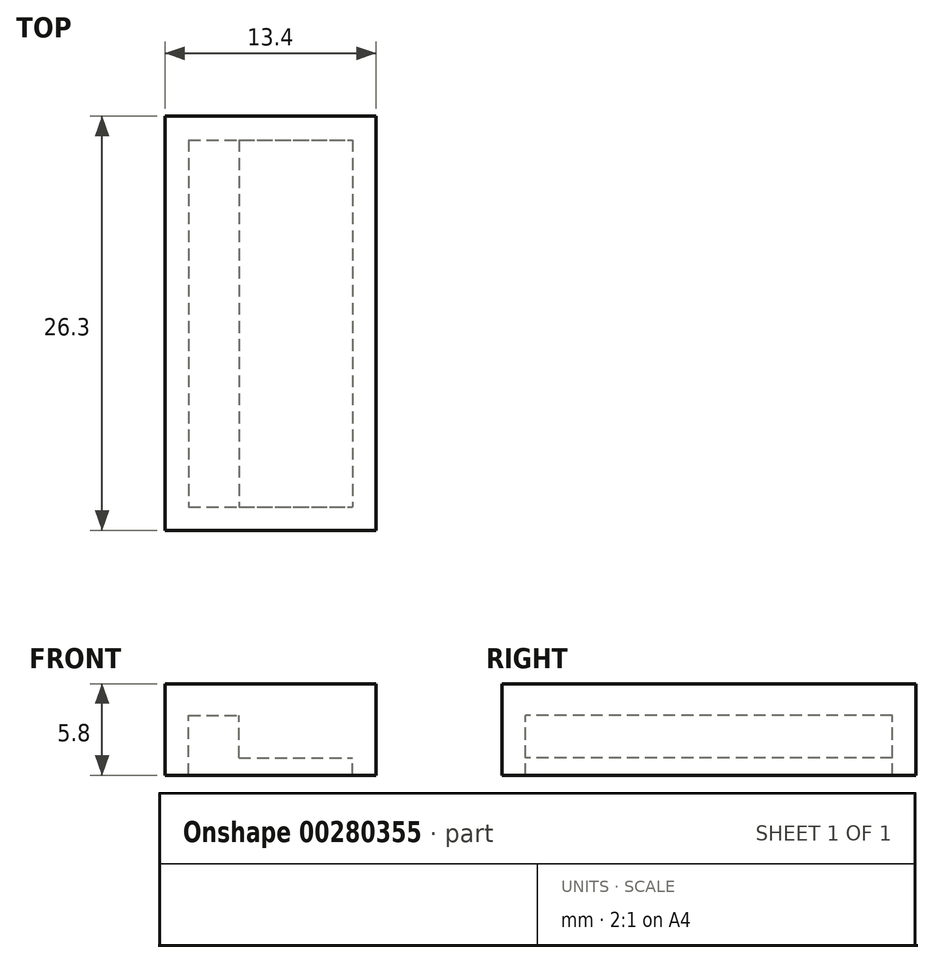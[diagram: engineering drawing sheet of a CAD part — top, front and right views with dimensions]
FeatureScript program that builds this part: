
annotation { "Feature Type Name" : "Feature", "Feature Type Description" : "" }
export const myFeature = defineFeature(function(context is Context, id is Id, definition is map)
    precondition{}
    {
        {
            var Q0;
            Q0=qCreatedBy(makeId("Top.planeOp"),FACE);
            var sketch = newSketch(context, id + "F0", { "sketchPlane" : qUnion([Q0])});
            skLineSegment(sketch, "E0.bottom", {"start": v(-19.84, -7.55) * mm, "end": v(-9.44, -7.55) * mm});
            skLineSegment(sketch, "E0.top", {"start": v(-19.84, -30.85) * mm, "end": v(-9.44, -30.85) * mm});
            skLineSegment(sketch, "E0.left", {"start": v(-19.84, -7.55) * mm, "end": v(-19.84, -30.85) * mm});
            skLineSegment(sketch, "E0.right", {"start": v(-9.44, -7.55) * mm, "end": v(-9.44, -30.85) * mm});
            skLineSegment(sketch, "E1.bottom", {"start": v(-21.34, -6.05) * mm, "end": v(-7.94, -6.05) * mm});
            skLineSegment(sketch, "E1.top", {"start": v(-21.34, -32.35) * mm, "end": v(-7.94, -32.35) * mm});
            skLineSegment(sketch, "E1.left", {"start": v(-21.34, -6.05) * mm, "end": v(-21.34, -32.35) * mm});
            skLineSegment(sketch, "E1.right", {"start": v(-7.94, -6.05) * mm, "end": v(-7.94, -32.35) * mm});
            skLineSegment(sketch, "E2", {"start": v(-16.64, -7.55) * mm, "end": v(-16.64, -30.85) * mm});
            skSolve(sketch);
        }
        {
            var Q0;
            {var subQ4=sQuery(id+"F0.wireOp",EDGE,"E0.left");Q0=makeQuery(id+"F0.imprint","IMPRINT",FACE,{"disambiguationData":[TD([[makeQuery(id+"F0.imprint","IMPRINT",EDGE,{"derivedFrom":subQ4}),-1.0]])]});}
            extrude(context, id + "F1", {"entities" : qUnion([Q0]), "oppositeDirection" : true, "depth" : 5.8 * mm});
        }
        {
            var Q0;
            {var subQ0=sQuery(id+"F0.wireOp",EDGE,"E0.left");Q0=makeQuery(id+"F0.imprint","IMPRINT",FACE,{"disambiguationData":[TD([[makeQuery(id+"F0.imprint","IMPRINT",EDGE,{"derivedFrom":subQ0}),1.0]])]});}
            extrude(context, id + "F2", {"entities" : qUnion([Q0]), "operationType" : NewBodyOperationType.ADD, "oppositeDirection" : true, "depth" : 2 * mm});
        }
        {
            var Q0;
            {var subQ0=sQuery(id+"F0.wireOp",EDGE,"E0.right");Q0=makeQuery(id+"F0.imprint","IMPRINT",FACE,{"disambiguationData":[TD([[makeQuery(id+"F0.imprint","IMPRINT",EDGE,{"derivedFrom":subQ0}),-1.0]])]});}
            extrude(context, id + "F3", {"entities" : qUnion([Q0]), "operationType" : NewBodyOperationType.ADD, "oppositeDirection" : true, "depth" : 4.7 * mm});
        }
    });
